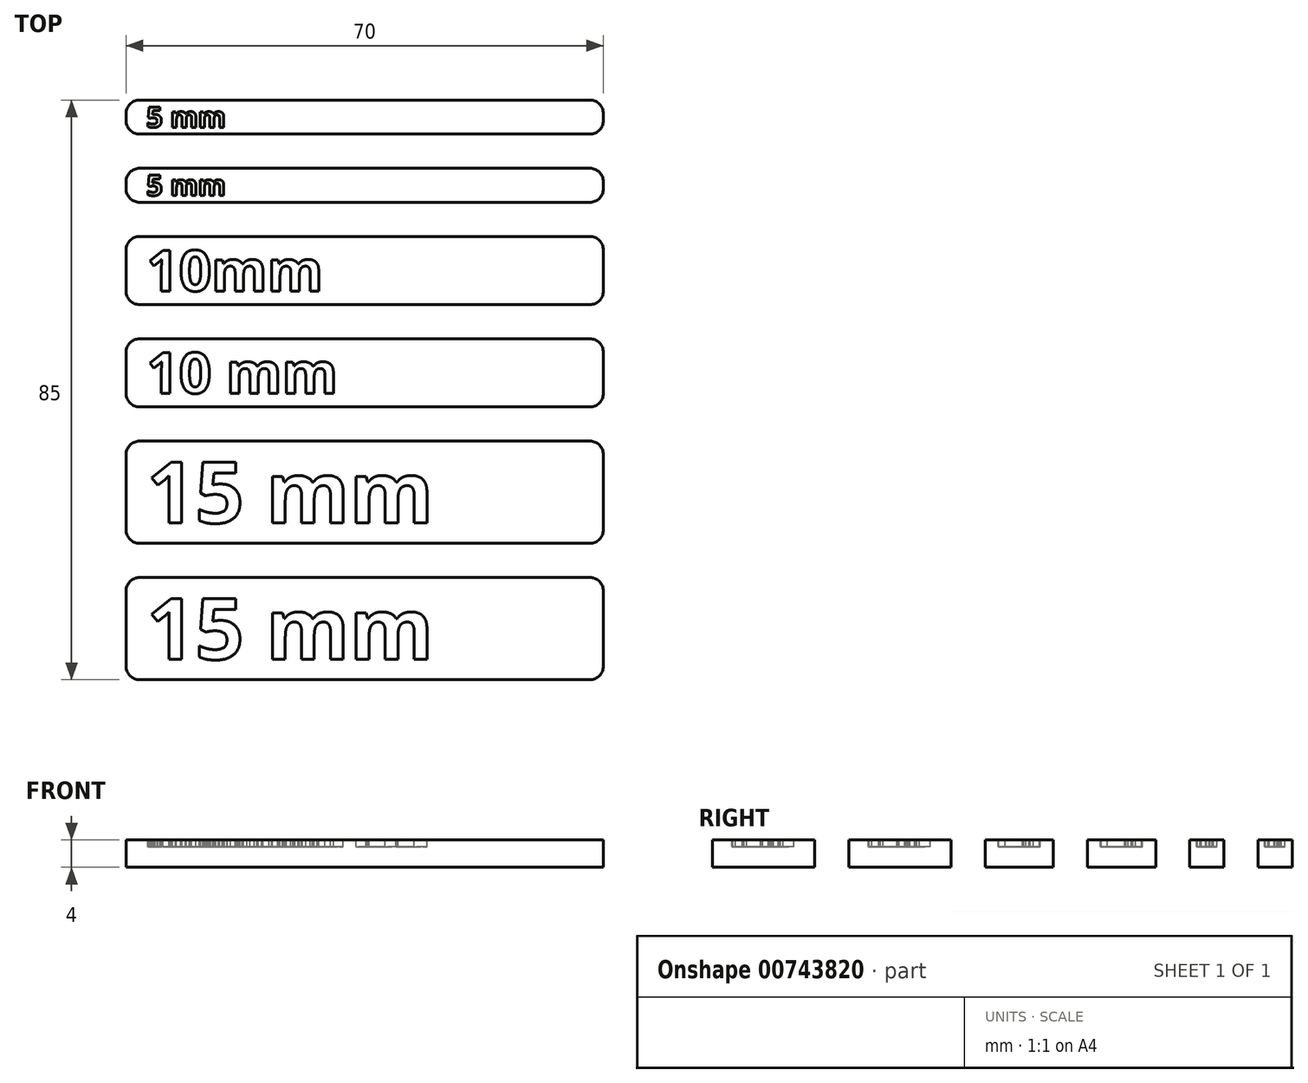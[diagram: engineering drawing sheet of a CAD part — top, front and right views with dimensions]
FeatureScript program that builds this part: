
annotation { "Feature Type Name" : "Feature", "Feature Type Description" : "" }
export const myFeature = defineFeature(function(context is Context, id is Id, definition is map)
    precondition{}
    {
        {
            var Q0;
            Q0=qCreatedBy(makeId("Top.planeOp"),FACE);
            var sketch = newSketch(context, id + "F0", { "sketchPlane" : qUnion([Q0])});
            skLineSegment(sketch, "E0.bottom", {"start": v(-35, 0) * mm, "end": v(35, 0) * mm});
            skLineSegment(sketch, "E0.top", {"start": v(-35, 5) * mm, "end": v(35, 5) * mm});
            skLineSegment(sketch, "E0.left", {"start": v(-35, 0) * mm, "end": v(-35, 5) * mm});
            skLineSegment(sketch, "E0.right", {"start": v(35, 0) * mm, "end": v(35, 5) * mm});
            skLineSegment(sketch, "E1.bottom", {"start": v(-35, 10) * mm, "end": v(35, 10) * mm});
            skLineSegment(sketch, "E1.top", {"start": v(-35, 15) * mm, "end": v(35, 15) * mm});
            skLineSegment(sketch, "E1.left", {"start": v(-35, 10) * mm, "end": v(-35, 15) * mm});
            skLineSegment(sketch, "E1.right", {"start": v(35, 10) * mm, "end": v(35, 15) * mm});
            skLineSegment(sketch, "E2.bottom", {"start": v(-35, -5) * mm, "end": v(35, -5) * mm});
            skLineSegment(sketch, "E2.top", {"start": v(-35, -15) * mm, "end": v(35, -15) * mm});
            skLineSegment(sketch, "E2.left", {"start": v(-35, -5) * mm, "end": v(-35, -15) * mm});
            skLineSegment(sketch, "E2.right", {"start": v(35, -5) * mm, "end": v(35, -15) * mm});
            skLineSegment(sketch, "E3.bottom", {"start": v(-35, -20) * mm, "end": v(35, -20) * mm});
            skLineSegment(sketch, "E3.top", {"start": v(-35, -30) * mm, "end": v(35, -30) * mm});
            skLineSegment(sketch, "E3.left", {"start": v(-35, -20) * mm, "end": v(-35, -30) * mm});
            skLineSegment(sketch, "E3.right", {"start": v(35, -20) * mm, "end": v(35, -30) * mm});
            skLineSegment(sketch, "E4.bottom", {"start": v(-35, -35) * mm, "end": v(35, -35) * mm});
            skLineSegment(sketch, "E4.top", {"start": v(-35, -50) * mm, "end": v(35, -50) * mm});
            skLineSegment(sketch, "E4.left", {"start": v(-35, -35) * mm, "end": v(-35, -50) * mm});
            skLineSegment(sketch, "E4.right", {"start": v(35, -35) * mm, "end": v(35, -50) * mm});
            skLineSegment(sketch, "E5.bottom", {"start": v(-35, -55) * mm, "end": v(35, -55) * mm});
            skLineSegment(sketch, "E5.top", {"start": v(-35, -70) * mm, "end": v(35, -70) * mm});
            skLineSegment(sketch, "E5.left", {"start": v(-35, -55) * mm, "end": v(-35, -70) * mm});
            skLineSegment(sketch, "E5.right", {"start": v(35, -55) * mm, "end": v(35, -70) * mm});
            skSolve(sketch);
        }
        {
            var Q0;
            Q0=makeQuery(id+"F0.imprint","IMPRINT",FACE,{"disambiguationData":[TD([[makeQuery(id+"F0.imprint","IMPRINT",EDGE,{"derivedFrom":sQuery(id+"F0.wireOp",EDGE,"E1.bottom")}),1.0]])]});
            var Q1;
            Q1=makeQuery(id+"F0.imprint","IMPRINT",FACE,{"disambiguationData":[TD([[makeQuery(id+"F0.imprint","IMPRINT",EDGE,{"derivedFrom":sQuery(id+"F0.wireOp",EDGE,"E0.bottom")}),1.0]])]});
            var Q2;
            Q2=makeQuery(id+"F0.imprint","IMPRINT",FACE,{"disambiguationData":[TD([[makeQuery(id+"F0.imprint","IMPRINT",EDGE,{"derivedFrom":sQuery(id+"F0.wireOp",EDGE,"E2.bottom")}),-1.0]])]});
            var Q3;
            Q3=makeQuery(id+"F0.imprint","IMPRINT",FACE,{"disambiguationData":[TD([[makeQuery(id+"F0.imprint","IMPRINT",EDGE,{"derivedFrom":sQuery(id+"F0.wireOp",EDGE,"E3.bottom")}),-1.0]])]});
            var Q4;
            Q4=makeQuery(id+"F0.imprint","IMPRINT",FACE,{"disambiguationData":[TD([[makeQuery(id+"F0.imprint","IMPRINT",EDGE,{"derivedFrom":sQuery(id+"F0.wireOp",EDGE,"E4.bottom")}),-1.0]])]});
            var Q5;
            Q5=makeQuery(id+"F0.imprint","IMPRINT",FACE,{"disambiguationData":[TD([[makeQuery(id+"F0.imprint","IMPRINT",EDGE,{"derivedFrom":sQuery(id+"F0.wireOp",EDGE,"E5.bottom")}),-1.0]])]});
            extrude(context, id + "F1", {"entities" : qUnion([Q0, Q1, Q2, Q3, Q4, Q5]), "depth" : 4 * mm, "offsetDistance" : 25 * mm});
        }
        {
            var Q0;
            Q0=makeQuery(id+"F1.opExtrude","CAP_FACE",FACE,{"disambiguationData":[OSD([sQuery(id+"F0.wireOp",EDGE,"E1.bottom"),sQuery(id+"F0.wireOp",EDGE,"E1.top"),sQuery(id+"F0.wireOp",EDGE,"E1.left"),sQuery(id+"F0.wireOp",EDGE,"E1.right")])],"isStart":false});
            var sketch = newSketch(context, id + "F2", { "sketchPlane" : qUnion([Q0])});
            skText(sketch, "E6", { "text": "15 mm", "fontName": "OpenSans-Bold.ttf"});
            skText(sketch, "E7", { "text": "10 mm", "fontName": "OpenSans-Bold.ttf"});
            skText(sketch, "E8", { "text": "5 mm", "fontName": "OpenSans-Bold.ttf"});
            skText(sketch, "E9", { "text": "15 mm", "fontName": "OpenSans-Bold.ttf"});
            skText(sketch, "E10", { "text": "10mm", "fontName": "OpenSans-Bold.ttf"});
            skText(sketch, "E11", { "text": "5 mm", "fontName": "OpenSans-Bold.ttf"});
            const initialGuessF2  = {"E6": [-0.032, -0.067, 1, 0, 0.009], "E7": [-0.032, -0.028, 1, 0, 0.006], "E8": [-0.032, 0.001, 1, 0, 0.003], "E9": [-0.032, -0.047, 1, 0, 0.009], "E10": [-0.032, -0.013, 1, 0, 0.006], "E11": [-0.032, 0.011, 1, 0, 0.003]};
            skSetInitialGuess(sketch, initialGuessF2);
            skSolve(sketch);
        }
        {
            var Q0;
            Q0 = qSketchRegion(id + "F2", true);
            extrude(context, id + "F3", {"entities" : qUnion([Q0]), "operationType" : NewBodyOperationType.REMOVE, "oppositeDirection" : true, "depth" : 1 * mm, "offsetDistance" : 25 * mm});
        }
        {
            var Q0;
            Q0=makeQuery(id+"F1.opExtrude","SWEPT_EDGE",EDGE,{"disambiguationData":[OSD([sQuery(id+"F0.wireOp",EDGE,"E1.top"),sQuery(id+"F0.wireOp",EDGE,"E1.left")])]});
            var Q1;
            Q1=makeQuery(id+"F1.opExtrude","SWEPT_EDGE",EDGE,{"disambiguationData":[OSD([sQuery(id+"F0.wireOp",EDGE,"E1.bottom"),sQuery(id+"F0.wireOp",EDGE,"E1.left")])]});
            var Q2;
            Q2=makeQuery(id+"F1.opExtrude","SWEPT_EDGE",EDGE,{"disambiguationData":[OSD([sQuery(id+"F0.wireOp",EDGE,"E0.top"),sQuery(id+"F0.wireOp",EDGE,"E0.left")])]});
            var Q3;
            Q3=makeQuery(id+"F1.opExtrude","SWEPT_EDGE",EDGE,{"disambiguationData":[OSD([sQuery(id+"F0.wireOp",EDGE,"E0.bottom"),sQuery(id+"F0.wireOp",EDGE,"E0.left")])]});
            var Q4;
            Q4=makeQuery(id+"F1.opExtrude","SWEPT_EDGE",EDGE,{"disambiguationData":[OSD([sQuery(id+"F0.wireOp",EDGE,"E2.bottom"),sQuery(id+"F0.wireOp",EDGE,"E2.left")])]});
            var Q5;
            Q5=makeQuery(id+"F1.opExtrude","SWEPT_EDGE",EDGE,{"disambiguationData":[OSD([sQuery(id+"F0.wireOp",EDGE,"E2.top"),sQuery(id+"F0.wireOp",EDGE,"E2.left")])]});
            var Q6;
            Q6=makeQuery(id+"F1.opExtrude","SWEPT_EDGE",EDGE,{"disambiguationData":[OSD([sQuery(id+"F0.wireOp",EDGE,"E3.bottom"),sQuery(id+"F0.wireOp",EDGE,"E3.left")])]});
            var Q7;
            Q7=makeQuery(id+"F1.opExtrude","SWEPT_EDGE",EDGE,{"disambiguationData":[OSD([sQuery(id+"F0.wireOp",EDGE,"E3.top"),sQuery(id+"F0.wireOp",EDGE,"E3.left")])]});
            var Q8;
            Q8=makeQuery(id+"F1.opExtrude","SWEPT_EDGE",EDGE,{"disambiguationData":[OSD([sQuery(id+"F0.wireOp",EDGE,"E4.bottom"),sQuery(id+"F0.wireOp",EDGE,"E4.left")])]});
            var Q9;
            Q9=makeQuery(id+"F1.opExtrude","SWEPT_EDGE",EDGE,{"disambiguationData":[OSD([sQuery(id+"F0.wireOp",EDGE,"E4.top"),sQuery(id+"F0.wireOp",EDGE,"E4.left")])]});
            var Q10;
            Q10=makeQuery(id+"F1.opExtrude","SWEPT_EDGE",EDGE,{"disambiguationData":[OSD([sQuery(id+"F0.wireOp",EDGE,"E5.bottom"),sQuery(id+"F0.wireOp",EDGE,"E5.left")])]});
            var Q11;
            Q11=makeQuery(id+"F1.opExtrude","SWEPT_EDGE",EDGE,{"disambiguationData":[OSD([sQuery(id+"F0.wireOp",EDGE,"E5.top"),sQuery(id+"F0.wireOp",EDGE,"E5.left")])]});
            var Q12;
            Q12=makeQuery(id+"F1.opExtrude","SWEPT_EDGE",EDGE,{"disambiguationData":[OSD([sQuery(id+"F0.wireOp",EDGE,"E1.top"),sQuery(id+"F0.wireOp",EDGE,"E1.right")])]});
            var Q13;
            Q13=makeQuery(id+"F1.opExtrude","SWEPT_EDGE",EDGE,{"disambiguationData":[OSD([sQuery(id+"F0.wireOp",EDGE,"E1.bottom"),sQuery(id+"F0.wireOp",EDGE,"E1.right")])]});
            var Q14;
            Q14=makeQuery(id+"F1.opExtrude","SWEPT_EDGE",EDGE,{"disambiguationData":[OSD([sQuery(id+"F0.wireOp",EDGE,"E0.top"),sQuery(id+"F0.wireOp",EDGE,"E0.right")])]});
            var Q15;
            Q15=makeQuery(id+"F1.opExtrude","SWEPT_EDGE",EDGE,{"disambiguationData":[OSD([sQuery(id+"F0.wireOp",EDGE,"E0.bottom"),sQuery(id+"F0.wireOp",EDGE,"E0.right")])]});
            var Q16;
            Q16=makeQuery(id+"F1.opExtrude","SWEPT_EDGE",EDGE,{"disambiguationData":[OSD([sQuery(id+"F0.wireOp",EDGE,"E2.bottom"),sQuery(id+"F0.wireOp",EDGE,"E2.right")])]});
            var Q17;
            Q17=makeQuery(id+"F1.opExtrude","SWEPT_EDGE",EDGE,{"disambiguationData":[OSD([sQuery(id+"F0.wireOp",EDGE,"E2.top"),sQuery(id+"F0.wireOp",EDGE,"E2.right")])]});
            var Q18;
            Q18=makeQuery(id+"F1.opExtrude","SWEPT_EDGE",EDGE,{"disambiguationData":[OSD([sQuery(id+"F0.wireOp",EDGE,"E3.bottom"),sQuery(id+"F0.wireOp",EDGE,"E3.right")])]});
            var Q19;
            Q19=makeQuery(id+"F1.opExtrude","SWEPT_EDGE",EDGE,{"disambiguationData":[OSD([sQuery(id+"F0.wireOp",EDGE,"E3.top"),sQuery(id+"F0.wireOp",EDGE,"E3.right")])]});
            var Q20;
            Q20=makeQuery(id+"F1.opExtrude","SWEPT_EDGE",EDGE,{"disambiguationData":[OSD([sQuery(id+"F0.wireOp",EDGE,"E4.bottom"),sQuery(id+"F0.wireOp",EDGE,"E4.right")])]});
            var Q21;
            Q21=makeQuery(id+"F1.opExtrude","SWEPT_EDGE",EDGE,{"disambiguationData":[OSD([sQuery(id+"F0.wireOp",EDGE,"E4.top"),sQuery(id+"F0.wireOp",EDGE,"E4.right")])]});
            var Q22;
            Q22=makeQuery(id+"F1.opExtrude","SWEPT_EDGE",EDGE,{"disambiguationData":[OSD([sQuery(id+"F0.wireOp",EDGE,"E5.bottom"),sQuery(id+"F0.wireOp",EDGE,"E5.right")])]});
            var Q23;
            Q23=makeQuery(id+"F1.opExtrude","SWEPT_EDGE",EDGE,{"disambiguationData":[OSD([sQuery(id+"F0.wireOp",EDGE,"E5.top"),sQuery(id+"F0.wireOp",EDGE,"E5.right")])]});
            fillet(context, id + "F4", {"entities" : qUnion([Q0, Q1, Q2, Q3, Q4, Q5, Q6, Q7, Q8, Q9, Q10, Q11, Q12, Q13, Q14, Q15, Q16, Q17, Q18, Q19, Q20, Q21, Q22, Q23]), "radius" : 2 * mm, "tangentPropagation" : true, "allowEdgeOverflow" : false});
        }
    });
